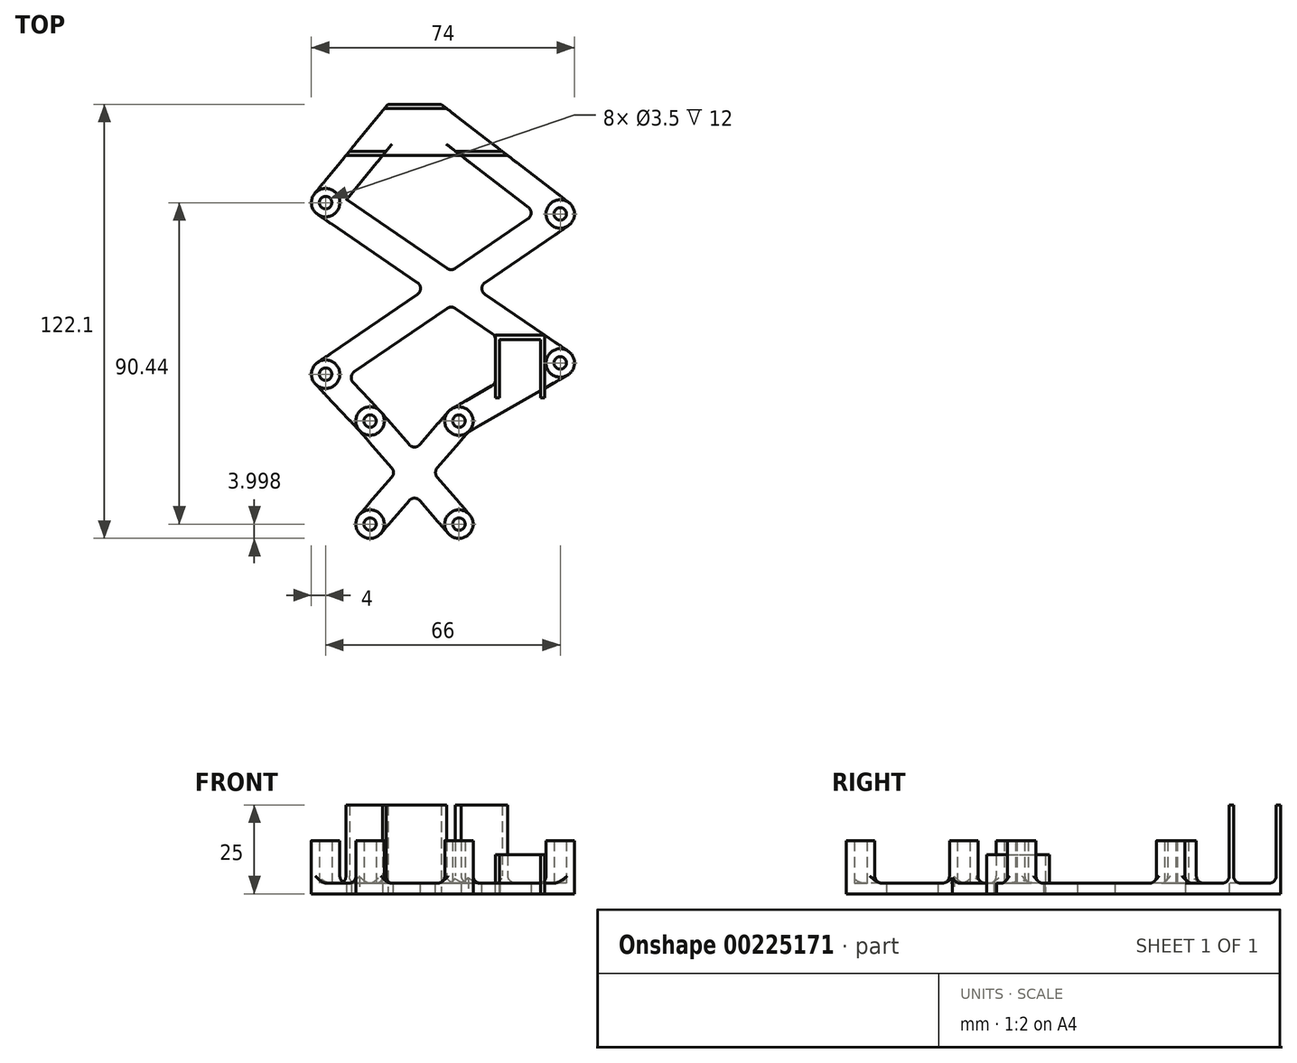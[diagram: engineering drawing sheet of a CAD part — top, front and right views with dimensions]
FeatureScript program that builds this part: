
annotation { "Feature Type Name" : "Feature", "Feature Type Description" : "" }
export const myFeature = defineFeature(function(context is Context, id is Id, definition is map)
    precondition{}
    {
        {
            var Q0;
            Q0=qCreatedBy(makeId("Top.planeOp"),FACE);
            var sketch = newSketch(context, id + "F0", { "sketchPlane" : qUnion([Q0])});
            skLineSegment(sketch, "E0.top", {"start": v(-0.5, 61.05) * mm, "end": v(-15.5, 61.05) * mm});
            skPoint(sketch, "E0.middle", {"position": v(0, 0) * mm});
            skCircle(sketch, "E1", {"center": v(33, 30.2) * mm, "radius": 4 * mm});
            skCircle(sketch, "E2", {"center": v(33, -11.7) * mm, "radius": 4 * mm});
            skCircle(sketch, "E3", {"center": v(-33, 33.39) * mm, "radius": 4 * mm});
            skCircle(sketch, "E4", {"center": v(-33, -14.87) * mm, "radius": 4 * mm});
            skLineSegment(sketch, "E5", {"start": v(-47.57, -18.05) * mm, "end": v(37, -18.05) * mm, "construction": true});
            skCircle(sketch, "E6", {"center": v(4.5, -28.05) * mm, "radius": 4 * mm});
            skCircle(sketch, "E7", {"center": v(4.5, -57.05) * mm, "radius": 4 * mm});
            skCircle(sketch, "E8", {"center": v(-20.5, -28.05) * mm, "radius": 4 * mm});
            skCircle(sketch, "E9", {"center": v(-20.5, -57.05) * mm, "radius": 4 * mm});
            skLineSegment(sketch, "E10", {"start": v(-20.5, -57.05) * mm, "end": v(4.5, -57.05) * mm, "construction": true});
            skLineSegment(sketch, "E11", {"start": v(-16.48, 59.85) * mm, "end": v(1.06, 59.85) * mm});
            skLineSegment(sketch, "E12", {"start": v(-26.32, 47.85) * mm, "end": v(16.64, 47.85) * mm});
            skLineSegment(sketch, "E13", {"start": v(-27.3, 46.65) * mm, "end": v(18.2, 46.65) * mm});
            skCircle(sketch, "E14", {"center": v(-33, 33.39) * mm, "radius": 1.75 * mm});
            skCircle(sketch, "E15", {"center": v(33, 30.2) * mm, "radius": 1.75 * mm});
            skCircle(sketch, "E16", {"center": v(33, -11.7) * mm, "radius": 1.75 * mm});
            skCircle(sketch, "E17", {"center": v(-33, -14.87) * mm, "radius": 1.75 * mm});
            skCircle(sketch, "E18", {"center": v(-20.5, -28.05) * mm, "radius": 1.75 * mm});
            skCircle(sketch, "E19", {"center": v(4.5, -28.05) * mm, "radius": 1.75 * mm});
            skCircle(sketch, "E20", {"center": v(4.5, -57.05) * mm, "radius": 1.75 * mm});
            skCircle(sketch, "E21", {"center": v(-20.5, -57.05) * mm, "radius": 1.75 * mm});
            skLineSegment(sketch, "E22", {"start": v(-30.74, 36.7) * mm, "end": v(35.26, -8.4) * mm});
            skLineSegment(sketch, "E23", {"start": v(-35.26, 30.08) * mm, "end": v(30.74, -15) * mm});
            skLineSegment(sketch, "E24", {"start": v(30.74, 33.51) * mm, "end": v(-35.26, -11.57) * mm});
            skLineSegment(sketch, "E25", {"start": v(35.26, 26.9) * mm, "end": v(-30.74, -18.18) * mm});
            skLineSegment(sketch, "E26", {"start": v(1.47, -25.44) * mm, "end": v(-23.53, -54.44) * mm});
            skLineSegment(sketch, "E27", {"start": v(7.53, -30.66) * mm, "end": v(-17.47, -59.66) * mm});
            skLineSegment(sketch, "E28", {"start": v(-17.47, -25.44) * mm, "end": v(7.53, -54.44) * mm});
            skLineSegment(sketch, "E29", {"start": v(-23.53, -30.66) * mm, "end": v(1.47, -59.66) * mm});
            skLineSegment(sketch, "E30", {"start": v(-36.1, 35.92) * mm, "end": v(-15.5, 61.05) * mm});
            skLineSegment(sketch, "E31", {"start": v(35.44, 33.38) * mm, "end": v(-0.5, 61.05) * mm});
            skPoint(sketch, "E32.orphan", {"position": v(-45, 61.05) * mm});
            skPoint(sketch, "E33.orphan", {"position": v(45, 61.05) * mm});
            skPoint(sketch, "E34", {"position": v(-8, 60.51) * mm});
            skLineSegment(sketch, "E35", {"start": v(-17.6, -25.3) * mm, "end": v(-30.1, -12.12) * mm});
            skLineSegment(sketch, "E36", {"start": v(-23.4, -30.8) * mm, "end": v(-35.9, -17.62) * mm});
            skLineSegment(sketch, "E37", {"start": v(2.5, -24.58) * mm, "end": v(31, -8.23) * mm});
            skLineSegment(sketch, "E38", {"start": v(35, -15.17) * mm, "end": v(6.5, -31.52) * mm});
            skPoint(sketch, "E39.orphan", {"position": v(-45, -61.05) * mm});
            skPoint(sketch, "E40.orphan", {"position": v(45, -61.05) * mm});
            skLineSegment(sketch, "E41", {"start": v(-29.9, 30.85) * mm, "end": v(-16.96, 46.65) * mm});
            skLineSegment(sketch, "E42", {"start": v(30.56, 27.04) * mm, "end": v(5.09, 46.65) * mm});
            skLineSegment(sketch, "E43", {"start": v(-16.96, 46.65) * mm, "end": v(-15.97, 47.85) * mm});
            skLineSegment(sketch, "E44", {"start": v(5.09, 46.65) * mm, "end": v(3.53, 47.85) * mm});
            skPoint(sketch, "E45", {"position": v(-8, -57.05) * mm});
            skPoint(sketch, "E46", {"position": v(-8, 61.05) * mm});
            skSolve(sketch);
        }
        {
            var Q0;
            {var subQ5=sQuery(id+"F0.wireOp",EDGE,"E22");var subQ6=sQuery(id+"F0.wireOp",EDGE,"E3");var subQ7=makeQuery(id+"F0.imprint","INTERSECT",VERTEX,{"derivedFrom":[subQ6,subQ5]});Q0=makeQuery(id+"F0.imprint","IMPRINT",FACE,{"disambiguationData":[TD([[makeQuery(id+"F0.imprint","IMPRINT",EDGE,{"disambiguationData":[TD([[subQ7,-1.0]])],"derivedFrom":subQ6}),-1.0]])]});}
            var Q1;
            {var subQ1=sQuery(id+"F0.wireOp",EDGE,"E23");var subQ5=sQuery(id+"F0.wireOp",EDGE,"E3");var subQ6=makeQuery(id+"F0.imprint","INTERSECT",VERTEX,{"derivedFrom":[subQ5,subQ1]});Q1=makeQuery(id+"F0.imprint","IMPRINT",FACE,{"disambiguationData":[TD([[makeQuery(id+"F0.imprint","IMPRINT",EDGE,{"disambiguationData":[TD([[subQ6,-1.0]])],"derivedFrom":subQ5}),-1.0]])]});}
            var Q2;
            {var subQ0=sQuery(id+"F0.wireOp",EDGE,"E0.top");Q2=makeQuery(id+"F0.imprint","IMPRINT",FACE,{"disambiguationData":[TD([[makeQuery(id+"F0.imprint","IMPRINT",EDGE,{"derivedFrom":subQ0}),1.0]])]});}
            var Q3;
            {var subQ0=sQuery(id+"F0.wireOp",EDGE,"E24");var subQ1=sQuery(id+"F0.wireOp",EDGE,"E1");var subQ2=makeQuery(id+"F0.imprint","INTERSECT",VERTEX,{"derivedFrom":[subQ1,subQ0]});Q3=makeQuery(id+"F0.imprint","IMPRINT",FACE,{"disambiguationData":[TD([[makeQuery(id+"F0.imprint","IMPRINT",EDGE,{"disambiguationData":[TD([[subQ2,-1.0]])],"derivedFrom":subQ1}),-1.0]])]});}
            var Q4;
            Q4=makeQuery(id+"F0.imprint","IMPRINT",FACE,{"disambiguationData":[TD([[makeQuery(id+"F0.imprint","IMPRINT",EDGE,{"derivedFrom":sQuery(id+"F0.wireOp",EDGE,"E15")}),-1.0]])]});
            var Q5;
            {var subQ0=sQuery(id+"F0.wireOp",EDGE,"E26");var subQ1=sQuery(id+"F0.wireOp",EDGE,"E6");var subQ2=makeQuery(id+"F0.imprint","INTERSECT",VERTEX,{"derivedFrom":[subQ1,subQ0]});Q5=makeQuery(id+"F0.imprint","IMPRINT",FACE,{"disambiguationData":[TD([[makeQuery(id+"F0.imprint","IMPRINT",EDGE,{"disambiguationData":[TD([[subQ2,-1.0]])],"derivedFrom":subQ1}),-1.0]])]});}
            var Q6;
            {var subQ0=sQuery(id+"F0.wireOp",EDGE,"E25");var subQ1=sQuery(id+"F0.wireOp",EDGE,"E4");var subQ2=makeQuery(id+"F0.imprint","INTERSECT",VERTEX,{"derivedFrom":[subQ1,subQ0]});Q6=makeQuery(id+"F0.imprint","IMPRINT",FACE,{"disambiguationData":[TD([[makeQuery(id+"F0.imprint","IMPRINT",EDGE,{"disambiguationData":[TD([[subQ2,-1.0]])],"derivedFrom":subQ1}),-1.0]])]});}
            var Q7;
            {var subQ4=sQuery(id+"F0.wireOp",EDGE,"E12");Q7=makeQuery(id+"F0.imprint","IMPRINT",FACE,{"disambiguationData":[TD([[makeQuery(id+"F0.imprint","IMPRINT",EDGE,{"derivedFrom":subQ4}),-1.0]])]});}
            var Q8;
            Q8=makeQuery(id+"F0.imprint","IMPRINT",FACE,{"disambiguationData":[TD([[makeQuery(id+"F0.imprint","IMPRINT",EDGE,{"derivedFrom":sQuery(id+"F0.wireOp",EDGE,"E17")}),-1.0]])]});
            var Q9;
            {var subQ5=sQuery(id+"F0.wireOp",EDGE,"E23");var subQ6=sQuery(id+"F0.wireOp",EDGE,"E2");var subQ7=makeQuery(id+"F0.imprint","INTERSECT",VERTEX,{"derivedFrom":[subQ6,subQ5]});Q9=makeQuery(id+"F0.imprint","IMPRINT",FACE,{"disambiguationData":[TD([[makeQuery(id+"F0.imprint","IMPRINT",EDGE,{"disambiguationData":[TD([[subQ7,-1.0]])],"derivedFrom":subQ6}),-1.0]])]});}
            var Q10;
            {var subQ0=sQuery(id+"F0.wireOp",EDGE,"E29");var subQ1=sQuery(id+"F0.wireOp",EDGE,"E8");var subQ2=makeQuery(id+"F0.imprint","INTERSECT",VERTEX,{"derivedFrom":[subQ1,subQ0]});Q10=makeQuery(id+"F0.imprint","IMPRINT",FACE,{"disambiguationData":[TD([[makeQuery(id+"F0.imprint","IMPRINT",EDGE,{"disambiguationData":[TD([[subQ2,-1.0]])],"derivedFrom":subQ1}),-1.0]])]});}
            var Q11;
            {var subQ0=sQuery(id+"F0.wireOp",EDGE,"E22");var subQ1=sQuery(id+"F0.wireOp",EDGE,"E3");var subQ2=makeQuery(id+"F0.imprint","INTERSECT",VERTEX,{"derivedFrom":[subQ1,subQ0]});Q11=makeQuery(id+"F0.imprint","IMPRINT",FACE,{"disambiguationData":[TD([[makeQuery(id+"F0.imprint","IMPRINT",EDGE,{"disambiguationData":[TD([[subQ2,1.0]])],"derivedFrom":subQ1}),-1.0]])]});}
            var Q12;
            {var subQ0=sQuery(id+"F0.wireOp",EDGE,"E11");Q12=makeQuery(id+"F0.imprint","IMPRINT",FACE,{"disambiguationData":[TD([[makeQuery(id+"F0.imprint","IMPRINT",EDGE,{"derivedFrom":subQ0}),-1.0]])]});}
            var Q13;
            {var subQ0=sQuery(id+"F0.wireOp",EDGE,"E23");var subQ1=sQuery(id+"F0.wireOp",EDGE,"E2");var subQ2=makeQuery(id+"F0.imprint","INTERSECT",VERTEX,{"derivedFrom":[subQ1,subQ0]});Q13=makeQuery(id+"F0.imprint","IMPRINT",FACE,{"disambiguationData":[TD([[makeQuery(id+"F0.imprint","IMPRINT",EDGE,{"disambiguationData":[TD([[subQ2,1.0]])],"derivedFrom":subQ1}),-1.0]])]});}
            var Q14;
            Q14=makeQuery(id+"F0.imprint","IMPRINT",FACE,{"disambiguationData":[TD([[makeQuery(id+"F0.imprint","IMPRINT",EDGE,{"derivedFrom":sQuery(id+"F0.wireOp",EDGE,"E20")}),-1.0]])]});
            var Q15;
            {var subQ0=sQuery(id+"F0.wireOp",EDGE,"E26");var subQ1=sQuery(id+"F0.wireOp",EDGE,"E9");var subQ2=makeQuery(id+"F0.imprint","INTERSECT",VERTEX,{"derivedFrom":[subQ1,subQ0]});Q15=makeQuery(id+"F0.imprint","IMPRINT",FACE,{"disambiguationData":[TD([[makeQuery(id+"F0.imprint","IMPRINT",EDGE,{"disambiguationData":[TD([[subQ2,1.0]])],"derivedFrom":subQ1}),-1.0]])]});}
            var Q16;
            Q16=makeQuery(id+"F0.imprint","IMPRINT",FACE,{"disambiguationData":[TD([[makeQuery(id+"F0.imprint","IMPRINT",EDGE,{"derivedFrom":sQuery(id+"F0.wireOp",EDGE,"E21")}),-1.0]])]});
            var Q17;
            {var subQ0=sQuery(id+"F0.wireOp",EDGE,"E28");var subQ1=sQuery(id+"F0.wireOp",EDGE,"E7");var subQ2=makeQuery(id+"F0.imprint","INTERSECT",VERTEX,{"derivedFrom":[subQ1,subQ0]});Q17=makeQuery(id+"F0.imprint","IMPRINT",FACE,{"disambiguationData":[TD([[makeQuery(id+"F0.imprint","IMPRINT",EDGE,{"disambiguationData":[TD([[subQ2,-1.0]])],"derivedFrom":subQ1}),-1.0]])]});}
            var Q18;
            {var subQ5=sQuery(id+"F0.wireOp",EDGE,"E25");var subQ6=sQuery(id+"F0.wireOp",EDGE,"E1");var subQ7=makeQuery(id+"F0.imprint","INTERSECT",VERTEX,{"derivedFrom":[subQ6,subQ5]});Q18=makeQuery(id+"F0.imprint","IMPRINT",FACE,{"disambiguationData":[TD([[makeQuery(id+"F0.imprint","IMPRINT",EDGE,{"disambiguationData":[TD([[subQ7,1.0]])],"derivedFrom":subQ6}),-1.0]])]});}
            var Q19;
            Q19=makeQuery(id+"F0.imprint","IMPRINT",FACE,{"disambiguationData":[TD([[makeQuery(id+"F0.imprint","IMPRINT",EDGE,{"derivedFrom":sQuery(id+"F0.wireOp",EDGE,"E16")}),-1.0]])]});
            var Q20;
            {var subQ3=sQuery(id+"F0.wireOp",EDGE,"E1");var subQ5=sQuery(id+"F0.wireOp",EDGE,"E24");var subQ6=makeQuery(id+"F0.imprint","INTERSECT",VERTEX,{"derivedFrom":[subQ3,subQ5]});Q20=makeQuery(id+"F0.imprint","IMPRINT",FACE,{"disambiguationData":[TD([[makeQuery(id+"F0.imprint","IMPRINT",EDGE,{"disambiguationData":[TD([[subQ6,1.0]])],"derivedFrom":subQ3}),-1.0]])]});}
            var Q21;
            {var subQ9=sQuery(id+"F0.wireOp",EDGE,"E36");Q21=makeQuery(id+"F0.imprint","IMPRINT",FACE,{"disambiguationData":[TD([[makeQuery(id+"F0.imprint","IMPRINT",EDGE,{"derivedFrom":subQ9}),-1.0]])]});}
            var Q22;
            Q22=makeQuery(id+"F0.imprint","IMPRINT",FACE,{"disambiguationData":[TD([[makeQuery(id+"F0.imprint","IMPRINT",EDGE,{"derivedFrom":sQuery(id+"F0.wireOp",EDGE,"E14")}),-1.0]])]});
            var Q23;
            {var subQ1=sQuery(id+"F0.wireOp",EDGE,"E22");var subQ5=sQuery(id+"F0.wireOp",EDGE,"E2");var subQ6=makeQuery(id+"F0.imprint","INTERSECT",VERTEX,{"derivedFrom":[subQ5,subQ1]});Q23=makeQuery(id+"F0.imprint","IMPRINT",FACE,{"disambiguationData":[TD([[makeQuery(id+"F0.imprint","IMPRINT",EDGE,{"disambiguationData":[TD([[subQ6,-1.0]])],"derivedFrom":subQ5}),-1.0]])]});}
            var Q24;
            {var subQ0=sQuery(id+"F0.wireOp",EDGE,"E25");var subQ1=sQuery(id+"F0.wireOp",EDGE,"E22");var subQ2=makeQuery(id+"F0.imprint","INTERSECT",VERTEX,{"derivedFrom":[subQ1,subQ0]});Q24=makeQuery(id+"F0.imprint","IMPRINT",FACE,{"disambiguationData":[TD([[makeQuery(id+"F0.imprint","IMPRINT",EDGE,{"disambiguationData":[TD([[subQ2,1.0]])],"derivedFrom":subQ1}),-1.0]])]});}
            var Q25;
            Q25=makeQuery(id+"F0.imprint","IMPRINT",FACE,{"disambiguationData":[TD([[makeQuery(id+"F0.imprint","IMPRINT",EDGE,{"derivedFrom":sQuery(id+"F0.wireOp",EDGE,"E18")}),-1.0]])]});
            var Q26;
            {var subQ0=sQuery(id+"F0.wireOp",EDGE,"E29");var subQ1=sQuery(id+"F0.wireOp",EDGE,"E26");var subQ2=makeQuery(id+"F0.imprint","INTERSECT",VERTEX,{"derivedFrom":[subQ1,subQ0]});Q26=makeQuery(id+"F0.imprint","IMPRINT",FACE,{"disambiguationData":[TD([[makeQuery(id+"F0.imprint","IMPRINT",EDGE,{"disambiguationData":[TD([[subQ2,1.0]])],"derivedFrom":subQ1}),1.0]])]});}
            var Q27;
            Q27=makeQuery(id+"F0.imprint","IMPRINT",FACE,{"disambiguationData":[TD([[makeQuery(id+"F0.imprint","IMPRINT",EDGE,{"derivedFrom":sQuery(id+"F0.wireOp",EDGE,"E19")}),-1.0]])]});
            var Q28;
            {var subQ0=sQuery(id+"F0.wireOp",EDGE,"E24");var subQ1=sQuery(id+"F0.wireOp",EDGE,"E4");var subQ2=makeQuery(id+"F0.imprint","INTERSECT",VERTEX,{"derivedFrom":[subQ1,subQ0]});Q28=makeQuery(id+"F0.imprint","IMPRINT",FACE,{"disambiguationData":[TD([[makeQuery(id+"F0.imprint","IMPRINT",EDGE,{"disambiguationData":[TD([[subQ2,1.0]])],"derivedFrom":subQ1}),-1.0]])]});}
            var Q29;
            Q29=makeQuery(id+"F0.imprint","IMPRINT",FACE,{"disambiguationData":[TD([[makeQuery(id+"F0.imprint","IMPRINT",EDGE,{"derivedFrom":sQuery(id+"F0.wireOp",EDGE,"E20")}),1.0]])]});
            var Q30;
            Q30=makeQuery(id+"F0.imprint","IMPRINT",FACE,{"disambiguationData":[TD([[makeQuery(id+"F0.imprint","IMPRINT",EDGE,{"derivedFrom":sQuery(id+"F0.wireOp",EDGE,"E21")}),1.0]])]});
            var Q31;
            Q31=makeQuery(id+"F0.imprint","IMPRINT",FACE,{"disambiguationData":[TD([[makeQuery(id+"F0.imprint","IMPRINT",EDGE,{"derivedFrom":sQuery(id+"F0.wireOp",EDGE,"E15")}),1.0]])]});
            var Q32;
            Q32=makeQuery(id+"F0.imprint","IMPRINT",FACE,{"disambiguationData":[TD([[makeQuery(id+"F0.imprint","IMPRINT",EDGE,{"derivedFrom":sQuery(id+"F0.wireOp",EDGE,"E18")}),1.0]])]});
            var Q33;
            Q33=makeQuery(id+"F0.imprint","IMPRINT",FACE,{"disambiguationData":[TD([[makeQuery(id+"F0.imprint","IMPRINT",EDGE,{"derivedFrom":sQuery(id+"F0.wireOp",EDGE,"E16")}),1.0]])]});
            var Q34;
            Q34=makeQuery(id+"F0.imprint","IMPRINT",FACE,{"disambiguationData":[TD([[makeQuery(id+"F0.imprint","IMPRINT",EDGE,{"derivedFrom":sQuery(id+"F0.wireOp",EDGE,"E14")}),1.0]])]});
            var Q35;
            Q35=makeQuery(id+"F0.imprint","IMPRINT",FACE,{"disambiguationData":[TD([[makeQuery(id+"F0.imprint","IMPRINT",EDGE,{"derivedFrom":sQuery(id+"F0.wireOp",EDGE,"E19")}),1.0]])]});
            var Q36;
            {var subQ0=sQuery(id+"F0.wireOp",EDGE,"E27");var subQ1=sQuery(id+"F0.wireOp",EDGE,"E6");var subQ2=makeQuery(id+"F0.imprint","INTERSECT",VERTEX,{"derivedFrom":[subQ1,subQ0]});Q36=makeQuery(id+"F0.imprint","IMPRINT",FACE,{"disambiguationData":[TD([[makeQuery(id+"F0.imprint","IMPRINT",EDGE,{"disambiguationData":[TD([[subQ2,1.0]])],"derivedFrom":subQ1}),-1.0]])]});}
            var Q37;
            Q37=makeQuery(id+"F0.imprint","IMPRINT",FACE,{"disambiguationData":[TD([[makeQuery(id+"F0.imprint","IMPRINT",EDGE,{"derivedFrom":sQuery(id+"F0.wireOp",EDGE,"E17")}),1.0]])]});
            var Q38;
            {var subQ0=sQuery(id+"F0.wireOp",EDGE,"E28");var subQ1=sQuery(id+"F0.wireOp",EDGE,"E8");var subQ2=makeQuery(id+"F0.imprint","INTERSECT",VERTEX,{"derivedFrom":[subQ1,subQ0]});Q38=makeQuery(id+"F0.imprint","IMPRINT",FACE,{"disambiguationData":[TD([[makeQuery(id+"F0.imprint","IMPRINT",EDGE,{"disambiguationData":[TD([[subQ2,1.0]])],"derivedFrom":subQ1}),-1.0]])]});}
            var Q39;
            {var subQ5=sQuery(id+"F0.wireOp",EDGE,"E25");var subQ6=sQuery(id+"F0.wireOp",EDGE,"E4");var subQ7=makeQuery(id+"F0.imprint","INTERSECT",VERTEX,{"derivedFrom":[subQ6,subQ5]});Q39=makeQuery(id+"F0.imprint","IMPRINT",FACE,{"disambiguationData":[TD([[makeQuery(id+"F0.imprint","IMPRINT",EDGE,{"disambiguationData":[TD([[subQ7,1.0]])],"derivedFrom":subQ6}),-1.0]])]});}
            extrude(context, id + "F1", {"entities" : qUnion([Q0, Q1, Q2, Q3, Q4, Q5, Q6, Q7, Q8, Q9, Q10, Q11, Q12, Q13, Q14, Q15, Q16, Q17, Q18, Q19, Q20, Q21, Q22, Q23, Q24, Q25, Q26, Q27, Q28, Q29, Q30, Q31, Q32, Q33, Q34, Q35, Q36, Q37, Q38, Q39]), "depth" : 3 * mm});
        }
        {
            var Q0;
            Q0=makeQuery(id+"F0.imprint","IMPRINT",FACE,{"disambiguationData":[TD([[makeQuery(id+"F0.imprint","IMPRINT",EDGE,{"derivedFrom":sQuery(id+"F0.wireOp",EDGE,"E3")}),1.0]])]});
            var Q1;
            Q1=makeQuery(id+"F0.imprint","IMPRINT",FACE,{"disambiguationData":[TD([[makeQuery(id+"F0.imprint","IMPRINT",EDGE,{"derivedFrom":sQuery(id+"F0.wireOp",EDGE,"E1")}),1.0]])]});
            var Q2;
            Q2=makeQuery(id+"F0.imprint","IMPRINT",FACE,{"disambiguationData":[TD([[makeQuery(id+"F0.imprint","IMPRINT",EDGE,{"derivedFrom":sQuery(id+"F0.wireOp",EDGE,"E2")}),1.0]])]});
            var Q3;
            Q3=makeQuery(id+"F0.imprint","IMPRINT",FACE,{"disambiguationData":[TD([[makeQuery(id+"F0.imprint","IMPRINT",EDGE,{"derivedFrom":sQuery(id+"F0.wireOp",EDGE,"E6")}),1.0]])]});
            var Q4;
            Q4=makeQuery(id+"F0.imprint","IMPRINT",FACE,{"disambiguationData":[TD([[makeQuery(id+"F0.imprint","IMPRINT",EDGE,{"derivedFrom":sQuery(id+"F0.wireOp",EDGE,"E8")}),1.0]])]});
            var Q5;
            Q5=makeQuery(id+"F0.imprint","IMPRINT",FACE,{"disambiguationData":[TD([[makeQuery(id+"F0.imprint","IMPRINT",EDGE,{"derivedFrom":sQuery(id+"F0.wireOp",EDGE,"E4")}),1.0]])]});
            var Q6;
            Q6=makeQuery(id+"F0.imprint","IMPRINT",FACE,{"disambiguationData":[TD([[makeQuery(id+"F0.imprint","IMPRINT",EDGE,{"derivedFrom":sQuery(id+"F0.wireOp",EDGE,"E9")}),1.0]])]});
            var Q7;
            Q7=makeQuery(id+"F0.imprint","IMPRINT",FACE,{"disambiguationData":[TD([[makeQuery(id+"F0.imprint","IMPRINT",EDGE,{"derivedFrom":sQuery(id+"F0.wireOp",EDGE,"E7")}),1.0]])]});
            extrude(context, id + "F2", {"entities" : qUnion([Q0, Q1, Q2, Q3, Q4, Q5, Q6, Q7]), "operationType" : NewBodyOperationType.ADD, "depth" : 15 * mm});
        }
        {
            var Q0;
            {var subQ3=sQuery(id+"F0.wireOp",EDGE,"E44");Q0=makeQuery(id+"F0.imprint","IMPRINT",FACE,{"disambiguationData":[TD([[makeQuery(id+"F0.imprint","IMPRINT",EDGE,{"derivedFrom":subQ3}),-1.0]])]});}
            var Q1;
            {var subQ3=sQuery(id+"F0.wireOp",EDGE,"E43");Q1=makeQuery(id+"F0.imprint","IMPRINT",FACE,{"disambiguationData":[TD([[makeQuery(id+"F0.imprint","IMPRINT",EDGE,{"derivedFrom":subQ3}),1.0]])]});}
            var Q2;
            {var subQ0=sQuery(id+"F0.wireOp",EDGE,"E0.top");Q2=makeQuery(id+"F0.imprint","IMPRINT",FACE,{"disambiguationData":[TD([[makeQuery(id+"F0.imprint","IMPRINT",EDGE,{"derivedFrom":subQ0}),1.0]])]});}
            extrude(context, id + "F3", {"entities" : qUnion([Q0, Q1, Q2]), "operationType" : NewBodyOperationType.ADD, "depth" : 25 * mm});
        }
        {
            var Q0;
            Q0=makeQuery(id+"FQK2rzAZHfowVvl_1.opFillet","SPLIT",FACE,{"disambiguationData":[OD(1.0)],"derivedFrom":makeQuery(id+"F1.opExtrude","CAP_FACE",FACE,{"disambiguationData":[OSD([sQuery(id+"F0.wireOp",EDGE,"E0.bottom"),sQuery(id+"F0.wireOp",EDGE,"E0.left"),sQuery(id+"F0.wireOp",EDGE,"E0.right"),sQuery(id+"F0.wireOp",EDGE,"E1"),sQuery(id+"F0.wireOp",EDGE,"E2"),sQuery(id+"F0.wireOp",EDGE,"E3"),sQuery(id+"F0.wireOp",EDGE,"E4"),sQuery(id+"F0.wireOp",EDGE,"E6"),sQuery(id+"F0.wireOp",EDGE,"E7"),sQuery(id+"F0.wireOp",EDGE,"E8"),sQuery(id+"F0.wireOp",EDGE,"E9"),sQuery(id+"F0.wireOp",EDGE,"E13")])],"isStart":false})});
            var sketch = newSketch(context, id + "F4", { "sketchPlane" : qUnion([Q0])});
            skLineSegment(sketch, "E47.bottom", {"start": v(15.95, -21.59) * mm, "end": v(15.95, -5.09) * mm});
            skLineSegment(sketch, "E47.top", {"start": v(27.45, -21.59) * mm, "end": v(27.45, -5.09) * mm});
            skLineSegment(sketch, "E47.right", {"start": v(15.95, -5.09) * mm, "end": v(27.45, -5.09) * mm});
            skPoint(sketch, "E47.middle", {"position": v(21.7, -13.34) * mm});
            skLineSegment(sketch, "E48.0", {"start": v(14.75, -3.89) * mm, "end": v(28.65, -3.89) * mm});
            skLineSegment(sketch, "E48.1", {"start": v(14.75, -21.59) * mm, "end": v(14.75, -3.89) * mm});
            skLineSegment(sketch, "E48.3", {"start": v(28.65, -21.59) * mm, "end": v(28.65, -3.89) * mm});
            skLineSegment(sketch, "E49", {"start": v(27.45, -21.59) * mm, "end": v(28.65, -21.59) * mm});
            skLineSegment(sketch, "E50", {"start": v(15.95, -21.59) * mm, "end": v(14.75, -21.59) * mm});
            skSolve(sketch);
        }
        {
            var Q0;
            {var subQ7=sQuery(id+"F4.wireOp",EDGE,"E47.right");var subQ9=sQuery(id+"F4.wireOp",EDGE,"E47.bottom");var subQ10=makeQuery(id+"F4.imprint","INTERSECT",VERTEX,{"derivedFrom":[subQ9,subQ7]});Q0=makeQuery(id+"F4.imprint","IMPRINT",FACE,{"disambiguationData":[TD([[makeQuery(id+"F4.imprint","IMPRINT",EDGE,{"disambiguationData":[TD([[subQ10,1.0]])],"derivedFrom":subQ9}),1.0]])]});}
            var Q1;
            {var subQ0=sQuery(id+"F4.wireOp",EDGE,"E50");Q1=makeQuery(id+"F4.imprint","IMPRINT",FACE,{"disambiguationData":[TD([[makeQuery(id+"F4.imprint","IMPRINT",EDGE,{"derivedFrom":subQ0}),-1.0]])]});}
            var Q2;
            {var subQ1=sQuery(id+"F4.wireOp",EDGE,"E48.0");Q2=makeQuery(id+"F4.imprint","IMPRINT",FACE,{"disambiguationData":[TD([[makeQuery(id+"F4.imprint","IMPRINT",EDGE,{"derivedFrom":subQ1}),-1.0]])]});}
            extrude(context, id + "F5", {"entities" : qUnion([Q0, Q1, Q2]), "operationType" : NewBodyOperationType.ADD, "depth" : 8 * mm, "hasSecondDirection" : true, "secondDirectionOppositeDirection" : true, "secondDirectionDepth" : 3 * mm});
        }
        {
            var Q0;
            {var subQ2=sQuery(id+"F0.wireOp",EDGE,"E37");var subQ13=sQuery(id+"F0.wireOp",EDGE,"E25");var subQ15=sQuery(id+"F0.wireOp",EDGE,"E23");Q0=makeQuery(id+"F5.boolean.opBoolean","SPLIT",FACE,{"disambiguationData":[TD([makeQuery(id+"F1.opExtrude","SWEPT_FACE",FACE,{"disambiguationData":[OSD([subQ2])]})])],"derivedFrom":makeQuery(id+"F1.opExtrude","SWEPT_FACE",FACE,{"disambiguationData":[OSD([subQ15]),TDD([makeQuery(id+"F0.imprint","IMPRINT",EDGE,{"disambiguationData":[TD([[makeQuery(id+"F0.imprint","INTERSECT",VERTEX,{"derivedFrom":[subQ15,subQ13]}),-1.0]])],"derivedFrom":subQ15})])]})});}
            extrude(context, id + "F6", {"entities" : qUnion([Q0]), "operationType" : NewBodyOperationType.ADD, "endBound" : BoundingType.UP_TO_NEXT, "depth" : 25 * mm});
        }
        {
            var Q0;
            {var subQ0=sQuery(id+"F0.wireOp",EDGE,"E3");Q0=makeQuery(id+"F2.boolean.opBoolean","INTERSECT",EDGE,{"derivedFrom":[makeQuery(id+"F1.opExtrude","CAP_FACE",FACE,{"disambiguationData":[OSD([sQuery(id+"F0.wireOp",EDGE,"E0.top"),sQuery(id+"F0.wireOp",EDGE,"E1"),sQuery(id+"F0.wireOp",EDGE,"E2"),subQ0,sQuery(id+"F0.wireOp",EDGE,"E4"),sQuery(id+"F0.wireOp",EDGE,"E6"),sQuery(id+"F0.wireOp",EDGE,"E7"),sQuery(id+"F0.wireOp",EDGE,"E8"),sQuery(id+"F0.wireOp",EDGE,"E9"),sQuery(id+"F0.wireOp",EDGE,"E13"),sQuery(id+"F0.wireOp",EDGE,"E22"),sQuery(id+"F0.wireOp",EDGE,"E23"),sQuery(id+"F0.wireOp",EDGE,"E24"),sQuery(id+"F0.wireOp",EDGE,"E25"),sQuery(id+"F0.wireOp",EDGE,"E26"),sQuery(id+"F0.wireOp",EDGE,"E27"),sQuery(id+"F0.wireOp",EDGE,"E28"),sQuery(id+"F0.wireOp",EDGE,"E29"),sQuery(id+"F0.wireOp",EDGE,"E30"),sQuery(id+"F0.wireOp",EDGE,"E31"),sQuery(id+"F0.wireOp",EDGE,"E35"),sQuery(id+"F0.wireOp",EDGE,"E36"),sQuery(id+"F0.wireOp",EDGE,"E37"),sQuery(id+"F0.wireOp",EDGE,"E38"),sQuery(id+"F0.wireOp",EDGE,"E41"),sQuery(id+"F0.wireOp",EDGE,"E42")])],"isStart":false}),makeQuery(id+"F2.opExtrude","SWEPT_FACE",FACE,{"disambiguationData":[OSD([subQ0])]})]});}
            var Q1;
            {var subQ0=sQuery(id+"F0.wireOp",EDGE,"E1");Q1=makeQuery(id+"F2.boolean.opBoolean","INTERSECT",EDGE,{"derivedFrom":[makeQuery(id+"F1.opExtrude","CAP_FACE",FACE,{"disambiguationData":[OSD([sQuery(id+"F0.wireOp",EDGE,"E0.top"),subQ0,sQuery(id+"F0.wireOp",EDGE,"E2"),sQuery(id+"F0.wireOp",EDGE,"E3"),sQuery(id+"F0.wireOp",EDGE,"E4"),sQuery(id+"F0.wireOp",EDGE,"E6"),sQuery(id+"F0.wireOp",EDGE,"E7"),sQuery(id+"F0.wireOp",EDGE,"E8"),sQuery(id+"F0.wireOp",EDGE,"E9"),sQuery(id+"F0.wireOp",EDGE,"E13"),sQuery(id+"F0.wireOp",EDGE,"E22"),sQuery(id+"F0.wireOp",EDGE,"E23"),sQuery(id+"F0.wireOp",EDGE,"E24"),sQuery(id+"F0.wireOp",EDGE,"E25"),sQuery(id+"F0.wireOp",EDGE,"E26"),sQuery(id+"F0.wireOp",EDGE,"E27"),sQuery(id+"F0.wireOp",EDGE,"E28"),sQuery(id+"F0.wireOp",EDGE,"E29"),sQuery(id+"F0.wireOp",EDGE,"E30"),sQuery(id+"F0.wireOp",EDGE,"E31"),sQuery(id+"F0.wireOp",EDGE,"E35"),sQuery(id+"F0.wireOp",EDGE,"E36"),sQuery(id+"F0.wireOp",EDGE,"E37"),sQuery(id+"F0.wireOp",EDGE,"E38"),sQuery(id+"F0.wireOp",EDGE,"E41"),sQuery(id+"F0.wireOp",EDGE,"E42")])],"isStart":false}),makeQuery(id+"F2.opExtrude","SWEPT_FACE",FACE,{"disambiguationData":[OSD([subQ0])]})]});}
            var Q2;
            {var subQ0=sQuery(id+"F0.wireOp",EDGE,"E2");Q2=makeQuery(id+"F2.boolean.opBoolean","INTERSECT",EDGE,{"derivedFrom":[makeQuery(id+"F1.opExtrude","CAP_FACE",FACE,{"disambiguationData":[OSD([sQuery(id+"F0.wireOp",EDGE,"E0.top"),sQuery(id+"F0.wireOp",EDGE,"E1"),subQ0,sQuery(id+"F0.wireOp",EDGE,"E3"),sQuery(id+"F0.wireOp",EDGE,"E4"),sQuery(id+"F0.wireOp",EDGE,"E6"),sQuery(id+"F0.wireOp",EDGE,"E7"),sQuery(id+"F0.wireOp",EDGE,"E8"),sQuery(id+"F0.wireOp",EDGE,"E9"),sQuery(id+"F0.wireOp",EDGE,"E13"),sQuery(id+"F0.wireOp",EDGE,"E22"),sQuery(id+"F0.wireOp",EDGE,"E23"),sQuery(id+"F0.wireOp",EDGE,"E24"),sQuery(id+"F0.wireOp",EDGE,"E25"),sQuery(id+"F0.wireOp",EDGE,"E26"),sQuery(id+"F0.wireOp",EDGE,"E27"),sQuery(id+"F0.wireOp",EDGE,"E28"),sQuery(id+"F0.wireOp",EDGE,"E29"),sQuery(id+"F0.wireOp",EDGE,"E30"),sQuery(id+"F0.wireOp",EDGE,"E31"),sQuery(id+"F0.wireOp",EDGE,"E35"),sQuery(id+"F0.wireOp",EDGE,"E36"),sQuery(id+"F0.wireOp",EDGE,"E37"),sQuery(id+"F0.wireOp",EDGE,"E38"),sQuery(id+"F0.wireOp",EDGE,"E41"),sQuery(id+"F0.wireOp",EDGE,"E42")])],"isStart":false}),makeQuery(id+"F2.opExtrude","SWEPT_FACE",FACE,{"disambiguationData":[OSD([subQ0])]})]});}
            var Q3;
            {var subQ0=sQuery(id+"F0.wireOp",EDGE,"E6");Q3=makeQuery(id+"F2.boolean.opBoolean","INTERSECT",EDGE,{"derivedFrom":[makeQuery(id+"F1.opExtrude","CAP_FACE",FACE,{"disambiguationData":[OSD([sQuery(id+"F0.wireOp",EDGE,"E0.top"),sQuery(id+"F0.wireOp",EDGE,"E1"),sQuery(id+"F0.wireOp",EDGE,"E2"),sQuery(id+"F0.wireOp",EDGE,"E3"),sQuery(id+"F0.wireOp",EDGE,"E4"),subQ0,sQuery(id+"F0.wireOp",EDGE,"E7"),sQuery(id+"F0.wireOp",EDGE,"E8"),sQuery(id+"F0.wireOp",EDGE,"E9"),sQuery(id+"F0.wireOp",EDGE,"E13"),sQuery(id+"F0.wireOp",EDGE,"E22"),sQuery(id+"F0.wireOp",EDGE,"E23"),sQuery(id+"F0.wireOp",EDGE,"E24"),sQuery(id+"F0.wireOp",EDGE,"E25"),sQuery(id+"F0.wireOp",EDGE,"E26"),sQuery(id+"F0.wireOp",EDGE,"E27"),sQuery(id+"F0.wireOp",EDGE,"E28"),sQuery(id+"F0.wireOp",EDGE,"E29"),sQuery(id+"F0.wireOp",EDGE,"E30"),sQuery(id+"F0.wireOp",EDGE,"E31"),sQuery(id+"F0.wireOp",EDGE,"E35"),sQuery(id+"F0.wireOp",EDGE,"E36"),sQuery(id+"F0.wireOp",EDGE,"E37"),sQuery(id+"F0.wireOp",EDGE,"E38"),sQuery(id+"F0.wireOp",EDGE,"E41"),sQuery(id+"F0.wireOp",EDGE,"E42")])],"isStart":false}),makeQuery(id+"F2.opExtrude","SWEPT_FACE",FACE,{"disambiguationData":[OSD([subQ0])]})]});}
            var Q4;
            {var subQ0=sQuery(id+"F0.wireOp",EDGE,"E4");Q4=makeQuery(id+"F2.boolean.opBoolean","INTERSECT",EDGE,{"derivedFrom":[makeQuery(id+"F1.opExtrude","CAP_FACE",FACE,{"disambiguationData":[OSD([sQuery(id+"F0.wireOp",EDGE,"E0.top"),sQuery(id+"F0.wireOp",EDGE,"E1"),sQuery(id+"F0.wireOp",EDGE,"E2"),sQuery(id+"F0.wireOp",EDGE,"E3"),subQ0,sQuery(id+"F0.wireOp",EDGE,"E6"),sQuery(id+"F0.wireOp",EDGE,"E7"),sQuery(id+"F0.wireOp",EDGE,"E8"),sQuery(id+"F0.wireOp",EDGE,"E9"),sQuery(id+"F0.wireOp",EDGE,"E13"),sQuery(id+"F0.wireOp",EDGE,"E22"),sQuery(id+"F0.wireOp",EDGE,"E23"),sQuery(id+"F0.wireOp",EDGE,"E24"),sQuery(id+"F0.wireOp",EDGE,"E25"),sQuery(id+"F0.wireOp",EDGE,"E26"),sQuery(id+"F0.wireOp",EDGE,"E27"),sQuery(id+"F0.wireOp",EDGE,"E28"),sQuery(id+"F0.wireOp",EDGE,"E29"),sQuery(id+"F0.wireOp",EDGE,"E30"),sQuery(id+"F0.wireOp",EDGE,"E31"),sQuery(id+"F0.wireOp",EDGE,"E35"),sQuery(id+"F0.wireOp",EDGE,"E36"),sQuery(id+"F0.wireOp",EDGE,"E37"),sQuery(id+"F0.wireOp",EDGE,"E38"),sQuery(id+"F0.wireOp",EDGE,"E41"),sQuery(id+"F0.wireOp",EDGE,"E42")])],"isStart":false}),makeQuery(id+"F2.opExtrude","SWEPT_FACE",FACE,{"disambiguationData":[OSD([subQ0])]})]});}
            var Q5;
            {var subQ0=sQuery(id+"F0.wireOp",EDGE,"E8");Q5=makeQuery(id+"F2.boolean.opBoolean","INTERSECT",EDGE,{"derivedFrom":[makeQuery(id+"F1.opExtrude","CAP_FACE",FACE,{"disambiguationData":[OSD([sQuery(id+"F0.wireOp",EDGE,"E0.top"),sQuery(id+"F0.wireOp",EDGE,"E1"),sQuery(id+"F0.wireOp",EDGE,"E2"),sQuery(id+"F0.wireOp",EDGE,"E3"),sQuery(id+"F0.wireOp",EDGE,"E4"),sQuery(id+"F0.wireOp",EDGE,"E6"),sQuery(id+"F0.wireOp",EDGE,"E7"),subQ0,sQuery(id+"F0.wireOp",EDGE,"E9"),sQuery(id+"F0.wireOp",EDGE,"E13"),sQuery(id+"F0.wireOp",EDGE,"E22"),sQuery(id+"F0.wireOp",EDGE,"E23"),sQuery(id+"F0.wireOp",EDGE,"E24"),sQuery(id+"F0.wireOp",EDGE,"E25"),sQuery(id+"F0.wireOp",EDGE,"E26"),sQuery(id+"F0.wireOp",EDGE,"E27"),sQuery(id+"F0.wireOp",EDGE,"E28"),sQuery(id+"F0.wireOp",EDGE,"E29"),sQuery(id+"F0.wireOp",EDGE,"E30"),sQuery(id+"F0.wireOp",EDGE,"E31"),sQuery(id+"F0.wireOp",EDGE,"E35"),sQuery(id+"F0.wireOp",EDGE,"E36"),sQuery(id+"F0.wireOp",EDGE,"E37"),sQuery(id+"F0.wireOp",EDGE,"E38"),sQuery(id+"F0.wireOp",EDGE,"E41"),sQuery(id+"F0.wireOp",EDGE,"E42")])],"isStart":false}),makeQuery(id+"F2.opExtrude","SWEPT_FACE",FACE,{"disambiguationData":[OSD([subQ0])]})]});}
            var Q6;
            {var subQ0=sQuery(id+"F0.wireOp",EDGE,"E9");Q6=makeQuery(id+"F2.boolean.opBoolean","INTERSECT",EDGE,{"derivedFrom":[makeQuery(id+"F1.opExtrude","CAP_FACE",FACE,{"disambiguationData":[OSD([sQuery(id+"F0.wireOp",EDGE,"E0.top"),sQuery(id+"F0.wireOp",EDGE,"E1"),sQuery(id+"F0.wireOp",EDGE,"E2"),sQuery(id+"F0.wireOp",EDGE,"E3"),sQuery(id+"F0.wireOp",EDGE,"E4"),sQuery(id+"F0.wireOp",EDGE,"E6"),sQuery(id+"F0.wireOp",EDGE,"E7"),sQuery(id+"F0.wireOp",EDGE,"E8"),subQ0,sQuery(id+"F0.wireOp",EDGE,"E13"),sQuery(id+"F0.wireOp",EDGE,"E22"),sQuery(id+"F0.wireOp",EDGE,"E23"),sQuery(id+"F0.wireOp",EDGE,"E24"),sQuery(id+"F0.wireOp",EDGE,"E25"),sQuery(id+"F0.wireOp",EDGE,"E26"),sQuery(id+"F0.wireOp",EDGE,"E27"),sQuery(id+"F0.wireOp",EDGE,"E28"),sQuery(id+"F0.wireOp",EDGE,"E29"),sQuery(id+"F0.wireOp",EDGE,"E30"),sQuery(id+"F0.wireOp",EDGE,"E31"),sQuery(id+"F0.wireOp",EDGE,"E35"),sQuery(id+"F0.wireOp",EDGE,"E36"),sQuery(id+"F0.wireOp",EDGE,"E37"),sQuery(id+"F0.wireOp",EDGE,"E38"),sQuery(id+"F0.wireOp",EDGE,"E41"),sQuery(id+"F0.wireOp",EDGE,"E42")])],"isStart":false}),makeQuery(id+"F2.opExtrude","SWEPT_FACE",FACE,{"disambiguationData":[OSD([subQ0])]})]});}
            var Q7;
            {var subQ0=sQuery(id+"F0.wireOp",EDGE,"E7");Q7=makeQuery(id+"F2.boolean.opBoolean","INTERSECT",EDGE,{"derivedFrom":[makeQuery(id+"F1.opExtrude","CAP_FACE",FACE,{"disambiguationData":[OSD([sQuery(id+"F0.wireOp",EDGE,"E0.top"),sQuery(id+"F0.wireOp",EDGE,"E1"),sQuery(id+"F0.wireOp",EDGE,"E2"),sQuery(id+"F0.wireOp",EDGE,"E3"),sQuery(id+"F0.wireOp",EDGE,"E4"),sQuery(id+"F0.wireOp",EDGE,"E6"),subQ0,sQuery(id+"F0.wireOp",EDGE,"E8"),sQuery(id+"F0.wireOp",EDGE,"E9"),sQuery(id+"F0.wireOp",EDGE,"E13"),sQuery(id+"F0.wireOp",EDGE,"E22"),sQuery(id+"F0.wireOp",EDGE,"E23"),sQuery(id+"F0.wireOp",EDGE,"E24"),sQuery(id+"F0.wireOp",EDGE,"E25"),sQuery(id+"F0.wireOp",EDGE,"E26"),sQuery(id+"F0.wireOp",EDGE,"E27"),sQuery(id+"F0.wireOp",EDGE,"E28"),sQuery(id+"F0.wireOp",EDGE,"E29"),sQuery(id+"F0.wireOp",EDGE,"E30"),sQuery(id+"F0.wireOp",EDGE,"E31"),sQuery(id+"F0.wireOp",EDGE,"E35"),sQuery(id+"F0.wireOp",EDGE,"E36"),sQuery(id+"F0.wireOp",EDGE,"E37"),sQuery(id+"F0.wireOp",EDGE,"E38"),sQuery(id+"F0.wireOp",EDGE,"E41"),sQuery(id+"F0.wireOp",EDGE,"E42")])],"isStart":false}),makeQuery(id+"F2.opExtrude","SWEPT_FACE",FACE,{"disambiguationData":[OSD([subQ0])]})]});}
            var Q8;
            {var subQ0=sQuery(id+"F0.wireOp",EDGE,"E38");var subQ1=sQuery(id+"F0.wireOp",EDGE,"E27");var subQ2=sQuery(id+"F0.wireOp",EDGE,"E28");var subQ4=sQuery(id+"F0.wireOp",EDGE,"E26");var subQ5=sQuery(id+"F0.wireOp",EDGE,"E9");var subQ6=sQuery(id+"F0.wireOp",EDGE,"E29");var subQ8=sQuery(id+"F0.wireOp",EDGE,"E6");var subQ10=sQuery(id+"F0.wireOp",EDGE,"E25");var subQ11=sQuery(id+"F0.wireOp",EDGE,"E23");var subQ13=sQuery(id+"F0.wireOp",EDGE,"E35");var subQ14=sQuery(id+"F0.wireOp",EDGE,"E1");var subQ15=sQuery(id+"F0.wireOp",EDGE,"E22");var subQ17=sQuery(id+"F0.wireOp",EDGE,"E24");var subQ18=sQuery(id+"F0.wireOp",EDGE,"E4");var subQ21=sQuery(id+"F0.wireOp",EDGE,"E42");var subQ22=sQuery(id+"F0.wireOp",EDGE,"E37");var subQ23=sQuery(id+"F0.wireOp",EDGE,"E3");var subQ24=sQuery(id+"F0.wireOp",EDGE,"E2");var subQ25=sQuery(id+"F0.wireOp",EDGE,"E41");var subQ27=sQuery(id+"F0.wireOp",EDGE,"E0.top");var subQ28=sQuery(id+"F0.wireOp",EDGE,"E13");var subQ29=sQuery(id+"F0.wireOp",EDGE,"E7");var subQ30=sQuery(id+"F0.wireOp",EDGE,"E8");var subQ31=sQuery(id+"F0.wireOp",EDGE,"E36");var subQ32=sQuery(id+"F0.wireOp",EDGE,"E30");var subQ33=sQuery(id+"F0.wireOp",EDGE,"E31");Q8=makeQuery(id+"F3.boolean.opBoolean","INTERSECT",EDGE,{"derivedFrom":[makeQuery(id+"F2.boolean.opBoolean","SPLIT",FACE,{"disambiguationData":[TD([makeQuery(id+"F1.opExtrude","SWEPT_FACE",FACE,{"disambiguationData":[OSD([subQ27])]})])],"derivedFrom":makeQuery(id+"F1.opExtrude","CAP_FACE",FACE,{"disambiguationData":[OSD([subQ27,subQ14,subQ24,subQ23,subQ18,subQ8,subQ29,subQ30,subQ5,subQ28,subQ15,subQ11,subQ17,subQ10,subQ4,subQ1,subQ2,subQ6,subQ32,subQ33,subQ13,subQ31,subQ22,subQ0,subQ25,subQ21])],"isStart":false})}),makeQuery(id+"F3.opExtrude","SWEPT_FACE",FACE,{"disambiguationData":[OSD([sQuery(id+"F0.wireOp",EDGE,"E11")])]})]});}
            var Q9;
            {var subQ0=sQuery(id+"F0.wireOp",EDGE,"E30");var subQ1=sQuery(id+"F0.wireOp",EDGE,"E13");var subQ2=sQuery(id+"F0.wireOp",EDGE,"E41");var subQ3=sQuery(id+"F0.wireOp",EDGE,"E38");var subQ4=sQuery(id+"F0.wireOp",EDGE,"E27");var subQ5=sQuery(id+"F0.wireOp",EDGE,"E28");var subQ7=sQuery(id+"F0.wireOp",EDGE,"E26");var subQ8=sQuery(id+"F0.wireOp",EDGE,"E9");var subQ9=sQuery(id+"F0.wireOp",EDGE,"E29");var subQ11=sQuery(id+"F0.wireOp",EDGE,"E6");var subQ13=sQuery(id+"F0.wireOp",EDGE,"E25");var subQ14=sQuery(id+"F0.wireOp",EDGE,"E23");var subQ16=sQuery(id+"F0.wireOp",EDGE,"E35");var subQ17=sQuery(id+"F0.wireOp",EDGE,"E1");var subQ18=sQuery(id+"F0.wireOp",EDGE,"E22");var subQ20=sQuery(id+"F0.wireOp",EDGE,"E24");var subQ21=sQuery(id+"F0.wireOp",EDGE,"E4");var subQ24=sQuery(id+"F0.wireOp",EDGE,"E42");var subQ25=sQuery(id+"F0.wireOp",EDGE,"E37");var subQ26=sQuery(id+"F0.wireOp",EDGE,"E3");var subQ27=sQuery(id+"F0.wireOp",EDGE,"E2");var subQ29=sQuery(id+"F0.wireOp",EDGE,"E0.top");var subQ30=sQuery(id+"F0.wireOp",EDGE,"E7");var subQ31=sQuery(id+"F0.wireOp",EDGE,"E8");var subQ32=sQuery(id+"F0.wireOp",EDGE,"E36");var subQ33=sQuery(id+"F0.wireOp",EDGE,"E31");Q9=makeQuery(id+"F3.boolean.opBoolean","INTERSECT",EDGE,{"derivedFrom":[makeQuery(id+"F2.boolean.opBoolean","SPLIT",FACE,{"disambiguationData":[TD([makeQuery(id+"F1.opExtrude","SWEPT_FACE",FACE,{"disambiguationData":[OSD([subQ29])]})])],"derivedFrom":makeQuery(id+"F1.opExtrude","CAP_FACE",FACE,{"disambiguationData":[OSD([subQ29,subQ17,subQ27,subQ26,subQ21,subQ11,subQ30,subQ31,subQ8,subQ1,subQ18,subQ14,subQ20,subQ13,subQ7,subQ4,subQ5,subQ9,subQ0,subQ33,subQ16,subQ32,subQ25,subQ3,subQ2,subQ24])],"isStart":false})}),makeQuery(id+"F3.opExtrude","SWEPT_FACE",FACE,{"disambiguationData":[OSD([subQ1]),TDD([makeQuery(id+"F0.imprint","IMPRINT",EDGE,{"disambiguationData":[TD([[makeQuery(id+"F0.imprint","INTERSECT",VERTEX,{"derivedFrom":[subQ1,subQ0]}),-1.0]])],"derivedFrom":subQ1})])]})]});}
            var Q10;
            {var subQ0=sQuery(id+"F0.wireOp",EDGE,"E31");var subQ1=sQuery(id+"F0.wireOp",EDGE,"E13");var subQ2=sQuery(id+"F0.wireOp",EDGE,"E42");var subQ3=sQuery(id+"F0.wireOp",EDGE,"E38");var subQ4=sQuery(id+"F0.wireOp",EDGE,"E27");var subQ5=sQuery(id+"F0.wireOp",EDGE,"E28");var subQ7=sQuery(id+"F0.wireOp",EDGE,"E26");var subQ8=sQuery(id+"F0.wireOp",EDGE,"E9");var subQ9=sQuery(id+"F0.wireOp",EDGE,"E29");var subQ11=sQuery(id+"F0.wireOp",EDGE,"E6");var subQ13=sQuery(id+"F0.wireOp",EDGE,"E25");var subQ14=sQuery(id+"F0.wireOp",EDGE,"E23");var subQ16=sQuery(id+"F0.wireOp",EDGE,"E35");var subQ17=sQuery(id+"F0.wireOp",EDGE,"E1");var subQ18=sQuery(id+"F0.wireOp",EDGE,"E22");var subQ20=sQuery(id+"F0.wireOp",EDGE,"E24");var subQ21=sQuery(id+"F0.wireOp",EDGE,"E4");var subQ24=sQuery(id+"F0.wireOp",EDGE,"E37");var subQ25=sQuery(id+"F0.wireOp",EDGE,"E3");var subQ26=sQuery(id+"F0.wireOp",EDGE,"E2");var subQ27=sQuery(id+"F0.wireOp",EDGE,"E41");var subQ29=sQuery(id+"F0.wireOp",EDGE,"E0.top");var subQ30=sQuery(id+"F0.wireOp",EDGE,"E7");var subQ31=sQuery(id+"F0.wireOp",EDGE,"E8");var subQ32=sQuery(id+"F0.wireOp",EDGE,"E36");var subQ33=sQuery(id+"F0.wireOp",EDGE,"E30");Q10=makeQuery(id+"F3.boolean.opBoolean","INTERSECT",EDGE,{"derivedFrom":[makeQuery(id+"F2.boolean.opBoolean","SPLIT",FACE,{"disambiguationData":[TD([makeQuery(id+"F1.opExtrude","SWEPT_FACE",FACE,{"disambiguationData":[OSD([subQ29])]})])],"derivedFrom":makeQuery(id+"F1.opExtrude","CAP_FACE",FACE,{"disambiguationData":[OSD([subQ29,subQ17,subQ26,subQ25,subQ21,subQ11,subQ30,subQ31,subQ8,subQ1,subQ18,subQ14,subQ20,subQ13,subQ7,subQ4,subQ5,subQ9,subQ33,subQ0,subQ16,subQ32,subQ24,subQ3,subQ27,subQ2])],"isStart":false})}),makeQuery(id+"F3.opExtrude","SWEPT_FACE",FACE,{"disambiguationData":[OSD([subQ1]),TDD([makeQuery(id+"F0.imprint","IMPRINT",EDGE,{"disambiguationData":[TD([[makeQuery(id+"F0.imprint","INTERSECT",VERTEX,{"derivedFrom":[subQ1,subQ0]}),1.0]])],"derivedFrom":subQ1})])]})]});}
            var Q11;
            {var subQ0=sQuery(id+"F0.wireOp",EDGE,"E31");var subQ1=sQuery(id+"F0.wireOp",EDGE,"E12");var subQ2=sQuery(id+"F0.wireOp",EDGE,"E38");var subQ3=sQuery(id+"F0.wireOp",EDGE,"E27");var subQ4=sQuery(id+"F0.wireOp",EDGE,"E28");var subQ6=sQuery(id+"F0.wireOp",EDGE,"E26");var subQ7=sQuery(id+"F0.wireOp",EDGE,"E9");var subQ8=sQuery(id+"F0.wireOp",EDGE,"E29");var subQ10=sQuery(id+"F0.wireOp",EDGE,"E6");var subQ12=sQuery(id+"F0.wireOp",EDGE,"E25");var subQ13=sQuery(id+"F0.wireOp",EDGE,"E23");var subQ15=sQuery(id+"F0.wireOp",EDGE,"E35");var subQ16=sQuery(id+"F0.wireOp",EDGE,"E1");var subQ17=sQuery(id+"F0.wireOp",EDGE,"E22");var subQ19=sQuery(id+"F0.wireOp",EDGE,"E24");var subQ20=sQuery(id+"F0.wireOp",EDGE,"E4");var subQ23=sQuery(id+"F0.wireOp",EDGE,"E42");var subQ24=sQuery(id+"F0.wireOp",EDGE,"E37");var subQ25=sQuery(id+"F0.wireOp",EDGE,"E3");var subQ26=sQuery(id+"F0.wireOp",EDGE,"E2");var subQ27=sQuery(id+"F0.wireOp",EDGE,"E41");var subQ29=sQuery(id+"F0.wireOp",EDGE,"E0.top");var subQ30=sQuery(id+"F0.wireOp",EDGE,"E13");var subQ31=sQuery(id+"F0.wireOp",EDGE,"E7");var subQ32=sQuery(id+"F0.wireOp",EDGE,"E8");var subQ33=sQuery(id+"F0.wireOp",EDGE,"E36");var subQ34=sQuery(id+"F0.wireOp",EDGE,"E30");Q11=makeQuery(id+"F3.boolean.opBoolean","INTERSECT",EDGE,{"derivedFrom":[makeQuery(id+"F2.boolean.opBoolean","SPLIT",FACE,{"disambiguationData":[TD([makeQuery(id+"F1.opExtrude","SWEPT_FACE",FACE,{"disambiguationData":[OSD([subQ29])]})])],"derivedFrom":makeQuery(id+"F1.opExtrude","CAP_FACE",FACE,{"disambiguationData":[OSD([subQ29,subQ16,subQ26,subQ25,subQ20,subQ10,subQ31,subQ32,subQ7,subQ30,subQ17,subQ13,subQ19,subQ12,subQ6,subQ3,subQ4,subQ8,subQ34,subQ0,subQ15,subQ33,subQ24,subQ2,subQ27,subQ23])],"isStart":false})}),makeQuery(id+"F3.opExtrude","SWEPT_FACE",FACE,{"disambiguationData":[OSD([subQ1]),TDD([makeQuery(id+"F0.imprint","IMPRINT",EDGE,{"disambiguationData":[TD([[makeQuery(id+"F0.imprint","INTERSECT",VERTEX,{"derivedFrom":[subQ1,subQ0]}),1.0]])],"derivedFrom":subQ1})])]})]});}
            var Q12;
            {var subQ0=sQuery(id+"F0.wireOp",EDGE,"E30");var subQ1=sQuery(id+"F0.wireOp",EDGE,"E12");var subQ2=sQuery(id+"F0.wireOp",EDGE,"E38");var subQ3=sQuery(id+"F0.wireOp",EDGE,"E27");var subQ4=sQuery(id+"F0.wireOp",EDGE,"E28");var subQ6=sQuery(id+"F0.wireOp",EDGE,"E26");var subQ7=sQuery(id+"F0.wireOp",EDGE,"E9");var subQ8=sQuery(id+"F0.wireOp",EDGE,"E29");var subQ10=sQuery(id+"F0.wireOp",EDGE,"E6");var subQ12=sQuery(id+"F0.wireOp",EDGE,"E25");var subQ13=sQuery(id+"F0.wireOp",EDGE,"E23");var subQ15=sQuery(id+"F0.wireOp",EDGE,"E35");var subQ16=sQuery(id+"F0.wireOp",EDGE,"E1");var subQ17=sQuery(id+"F0.wireOp",EDGE,"E22");var subQ19=sQuery(id+"F0.wireOp",EDGE,"E24");var subQ20=sQuery(id+"F0.wireOp",EDGE,"E4");var subQ23=sQuery(id+"F0.wireOp",EDGE,"E42");var subQ24=sQuery(id+"F0.wireOp",EDGE,"E37");var subQ25=sQuery(id+"F0.wireOp",EDGE,"E3");var subQ26=sQuery(id+"F0.wireOp",EDGE,"E2");var subQ27=sQuery(id+"F0.wireOp",EDGE,"E41");var subQ29=sQuery(id+"F0.wireOp",EDGE,"E0.top");var subQ30=sQuery(id+"F0.wireOp",EDGE,"E13");var subQ31=sQuery(id+"F0.wireOp",EDGE,"E7");var subQ32=sQuery(id+"F0.wireOp",EDGE,"E8");var subQ33=sQuery(id+"F0.wireOp",EDGE,"E36");var subQ34=sQuery(id+"F0.wireOp",EDGE,"E31");Q12=makeQuery(id+"F3.boolean.opBoolean","INTERSECT",EDGE,{"derivedFrom":[makeQuery(id+"F2.boolean.opBoolean","SPLIT",FACE,{"disambiguationData":[TD([makeQuery(id+"F1.opExtrude","SWEPT_FACE",FACE,{"disambiguationData":[OSD([subQ29])]})])],"derivedFrom":makeQuery(id+"F1.opExtrude","CAP_FACE",FACE,{"disambiguationData":[OSD([subQ29,subQ16,subQ26,subQ25,subQ20,subQ10,subQ31,subQ32,subQ7,subQ30,subQ17,subQ13,subQ19,subQ12,subQ6,subQ3,subQ4,subQ8,subQ0,subQ34,subQ15,subQ33,subQ24,subQ2,subQ27,subQ23])],"isStart":false})}),makeQuery(id+"F3.opExtrude","SWEPT_FACE",FACE,{"disambiguationData":[OSD([subQ1]),TDD([makeQuery(id+"F0.imprint","IMPRINT",EDGE,{"disambiguationData":[TD([[makeQuery(id+"F0.imprint","INTERSECT",VERTEX,{"derivedFrom":[subQ1,subQ0]}),-1.0]])],"derivedFrom":subQ1})])]})]});}
            var Q13;
            Q13=makeQuery(id+"F1.opExtrude","SWEPT_EDGE",EDGE,{"disambiguationData":[OSD([sQuery(id+"F0.wireOp",EDGE,"E24"),sQuery(id+"F0.wireOp",EDGE,"E42")])]});
            var Q14;
            Q14=makeQuery(id+"F1.opExtrude","SWEPT_EDGE",EDGE,{"disambiguationData":[OSD([sQuery(id+"F0.wireOp",EDGE,"E23"),sQuery(id+"F0.wireOp",EDGE,"E24")])]});
            var Q15;
            {var subQ0=sQuery(id+"F0.wireOp",EDGE,"E23");Q15=makeQuery(id+"F5.boolean.opBoolean","INTERSECT",EDGE,{"derivedFrom":[makeQuery(id+"F1.opExtrude","SWEPT_FACE",FACE,{"disambiguationData":[OSD([subQ0]),TDD([makeQuery(id+"F0.imprint","IMPRINT",EDGE,{"disambiguationData":[TD([[makeQuery(id+"F0.imprint","INTERSECT",VERTEX,{"derivedFrom":[subQ0,sQuery(id+"F0.wireOp",EDGE,"E25")]}),-1.0]])],"derivedFrom":subQ0})])]}),makeQuery(id+"F5.opExtrude","SWEPT_FACE",FACE,{"disambiguationData":[OSD([sQuery(id+"F4.wireOp",EDGE,"E48.1")])]})]});}
            var Q16;
            Q16=makeQuery(id+"F5.boolean.opBoolean","INTERSECT",EDGE,{"derivedFrom":[makeQuery(id+"F1.opExtrude","SWEPT_FACE",FACE,{"disambiguationData":[OSD([sQuery(id+"F0.wireOp",EDGE,"E37")])]}),makeQuery(id+"F5.opExtrude","SWEPT_FACE",FACE,{"disambiguationData":[OSD([sQuery(id+"F4.wireOp",EDGE,"E48.1")])]})]});
            var Q17;
            Q17=makeQuery(id+"F1.opExtrude","SWEPT_EDGE",EDGE,{"disambiguationData":[OSD([sQuery(id+"F0.wireOp",EDGE,"E22"),sQuery(id+"F0.wireOp",EDGE,"E25")])]});
            var Q18;
            Q18=makeQuery(id+"F1.opExtrude","SWEPT_EDGE",EDGE,{"disambiguationData":[OSD([sQuery(id+"F0.wireOp",EDGE,"E25"),sQuery(id+"F0.wireOp",EDGE,"E35")])]});
            var Q19;
            Q19=makeQuery(id+"F1.opExtrude","SWEPT_EDGE",EDGE,{"disambiguationData":[OSD([sQuery(id+"F0.wireOp",EDGE,"E23"),sQuery(id+"F0.wireOp",EDGE,"E25")])]});
            var Q20;
            Q20=makeQuery(id+"F1.opExtrude","SWEPT_EDGE",EDGE,{"disambiguationData":[OSD([sQuery(id+"F0.wireOp",EDGE,"E22"),sQuery(id+"F0.wireOp",EDGE,"E24")])]});
            var Q21;
            Q21=makeQuery(id+"F1.opExtrude","SWEPT_EDGE",EDGE,{"disambiguationData":[OSD([sQuery(id+"F0.wireOp",EDGE,"E26"),sQuery(id+"F0.wireOp",EDGE,"E28")])]});
            var Q22;
            Q22=makeQuery(id+"F1.opExtrude","SWEPT_EDGE",EDGE,{"disambiguationData":[OSD([sQuery(id+"F0.wireOp",EDGE,"E27"),sQuery(id+"F0.wireOp",EDGE,"E29")])]});
            var Q23;
            Q23=makeQuery(id+"F1.opExtrude","SWEPT_EDGE",EDGE,{"disambiguationData":[OSD([sQuery(id+"F0.wireOp",EDGE,"E27"),sQuery(id+"F0.wireOp",EDGE,"E28")])]});
            var Q24;
            Q24=makeQuery(id+"F1.opExtrude","SWEPT_EDGE",EDGE,{"disambiguationData":[OSD([sQuery(id+"F0.wireOp",EDGE,"E26"),sQuery(id+"F0.wireOp",EDGE,"E29")])]});
            fillet(context, id + "F7", {"entities" : qUnion([Q0, Q1, Q2, Q3, Q4, Q5, Q6, Q7, Q8, Q9, Q10, Q11, Q12, Q13, Q14, Q15, Q16, Q17, Q18, Q19, Q20, Q21, Q22, Q23, Q24]), "radius" : 2 * mm, "tangentPropagation" : true, "allowEdgeOverflow" : false});
        }
    });
